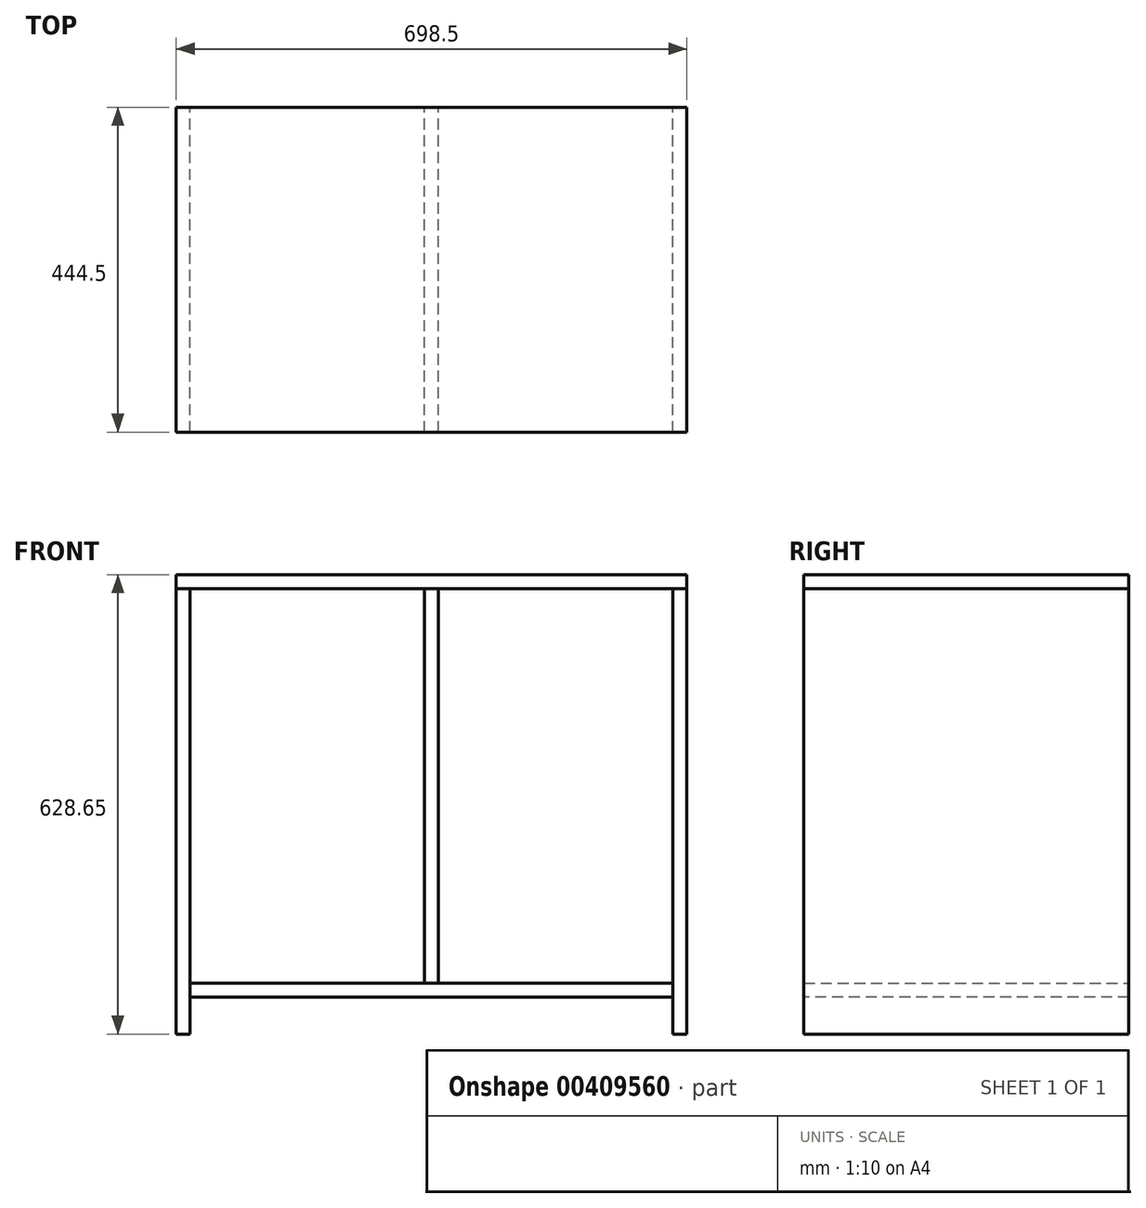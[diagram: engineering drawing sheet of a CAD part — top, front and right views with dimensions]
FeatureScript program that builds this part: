
annotation { "Feature Type Name" : "Feature", "Feature Type Description" : "" }
export const myFeature = defineFeature(function(context is Context, id is Id, definition is map)
    precondition{}
    {
        {
            var Q0;
            Q0=qCreatedBy(makeId("Top.planeOp"),FACE);
            var sketch = newSketch(context, id + "F0", { "sketchPlane" : qUnion([Q0])});
            skLineSegment(sketch, "E0.bottom", {"start": v(-330.2, 222.25) * mm, "end": v(330.2, 222.25) * mm});
            skLineSegment(sketch, "E0.top", {"start": v(-330.2, -222.25) * mm, "end": v(330.2, -222.25) * mm});
            skLineSegment(sketch, "E0.left", {"start": v(-330.2, 222.25) * mm, "end": v(-330.2, -222.25) * mm});
            skLineSegment(sketch, "E0.right", {"start": v(330.2, 222.25) * mm, "end": v(330.2, -222.25) * mm});
            skSolve(sketch);
        }
        {
            var Q0;
            Q0 = qSketchRegion(id + "F0", true);
            extrude(context, id + "F1", {"entities" : qUnion([Q0]), "depth" : 19.05 * mm});
        }
        {
            var Q0;
            Q0=makeQuery(id+"F1.opExtrude","SWEPT_FACE",FACE,{"disambiguationData":[OSD([sQuery(id+"F0.wireOp",EDGE,"E0.right")])]});
            var sketch = newSketch(context, id + "F2", { "sketchPlane" : qUnion([Q0])});
            skLineSegment(sketch, "E1.bottom", {"start": v(-222.25, -50.8) * mm, "end": v(222.25, -50.8) * mm});
            skLineSegment(sketch, "E1.top", {"start": v(-222.25, 558.8) * mm, "end": v(222.25, 558.8) * mm});
            skLineSegment(sketch, "E1.left", {"start": v(-222.25, -50.8) * mm, "end": v(-222.25, 558.8) * mm});
            skLineSegment(sketch, "E1.right", {"start": v(222.25, -50.8) * mm, "end": v(222.25, 558.8) * mm});
            skSolve(sketch);
        }
        {
            var Q0;
            Q0 = qSketchRegion(id + "F2", true);
            extrude(context, id + "F3", {"entities" : qUnion([Q0]), "depth" : 19.05 * mm});
        }
        {
            var Q0;
            Q0=makeQuery(id+"F3.opExtrude","SWEPT_BODY",BODY,{"disambiguationData":[OSD([sQuery(id+"F2.wireOp",EDGE,"E1.bottom"),sQuery(id+"F2.wireOp",EDGE,"E1.top"),sQuery(id+"F2.wireOp",EDGE,"E1.left"),sQuery(id+"F2.wireOp",EDGE,"E1.right")])]});
            var Q1;
            Q1=makeQuery(id+"F1.opExtrude","CAP_EDGE",EDGE,{"disambiguationData":[OSD([sQuery(id+"F0.wireOp",EDGE,"E0.top")])],"isStart":false});
            transform(context, id + "F4", {"entities" : qUnion([Q0]), "transformType" : TransformType.TRANSLATION_DISTANCE, "transformDirection" : qUnion([Q1]), "distance" : 679.45 * mm, "oppositeDirection" : true, "makeCopy" : true});
        }
        {
            var Q0;
            Q0=makeQuery(id+"F4.opPattern","COPY",FACE,{"derivedFrom":makeQuery(id+"F3.opExtrude","SWEPT_FACE",FACE,{"disambiguationData":[OSD([sQuery(id+"F2.wireOp",EDGE,"E1.top")])]}),"instanceName":"1"});
            var sketch = newSketch(context, id + "F5", { "sketchPlane" : qUnion([Q0])});
            skLineSegment(sketch, "E2.bottom", {"start": v(-349.25, -222.25) * mm, "end": v(349.25, -222.25) * mm});
            skLineSegment(sketch, "E2.top", {"start": v(-349.25, 222.25) * mm, "end": v(349.25, 222.25) * mm});
            skLineSegment(sketch, "E2.left", {"start": v(-349.25, -222.25) * mm, "end": v(-349.25, 222.25) * mm});
            skLineSegment(sketch, "E2.right", {"start": v(349.25, -222.25) * mm, "end": v(349.25, 222.25) * mm});
            skSolve(sketch);
        }
        {
            var Q0;
            Q0 = qSketchRegion(id + "F5", true);
            extrude(context, id + "F6", {"entities" : qUnion([Q0]), "depth" : 19.05 * mm});
        }
        {
            var Q0;
            Q0=qCreatedBy(makeId("Right.planeOp"),FACE);
            var sketch = newSketch(context, id + "F7", { "sketchPlane" : qUnion([Q0])});
            skLineSegment(sketch, "E3.bottom", {"start": v(-222.25, 19.05) * mm, "end": v(222.25, 19.05) * mm});
            skLineSegment(sketch, "E3.top", {"start": v(-222.25, 558.8) * mm, "end": v(222.25, 558.8) * mm});
            skLineSegment(sketch, "E3.left", {"start": v(-222.25, 19.05) * mm, "end": v(-222.25, 558.8) * mm});
            skLineSegment(sketch, "E3.right", {"start": v(222.25, 19.05) * mm, "end": v(222.25, 558.8) * mm});
            skSolve(sketch);
        }
        {
            var Q0;
            Q0 = qSketchRegion(id + "F7", true);
            extrude(context, id + "F8", {"entities" : qUnion([Q0]), "endBound" : BoundingType.SYMMETRIC, "depth" : 19.05 * mm});
        }
    });
